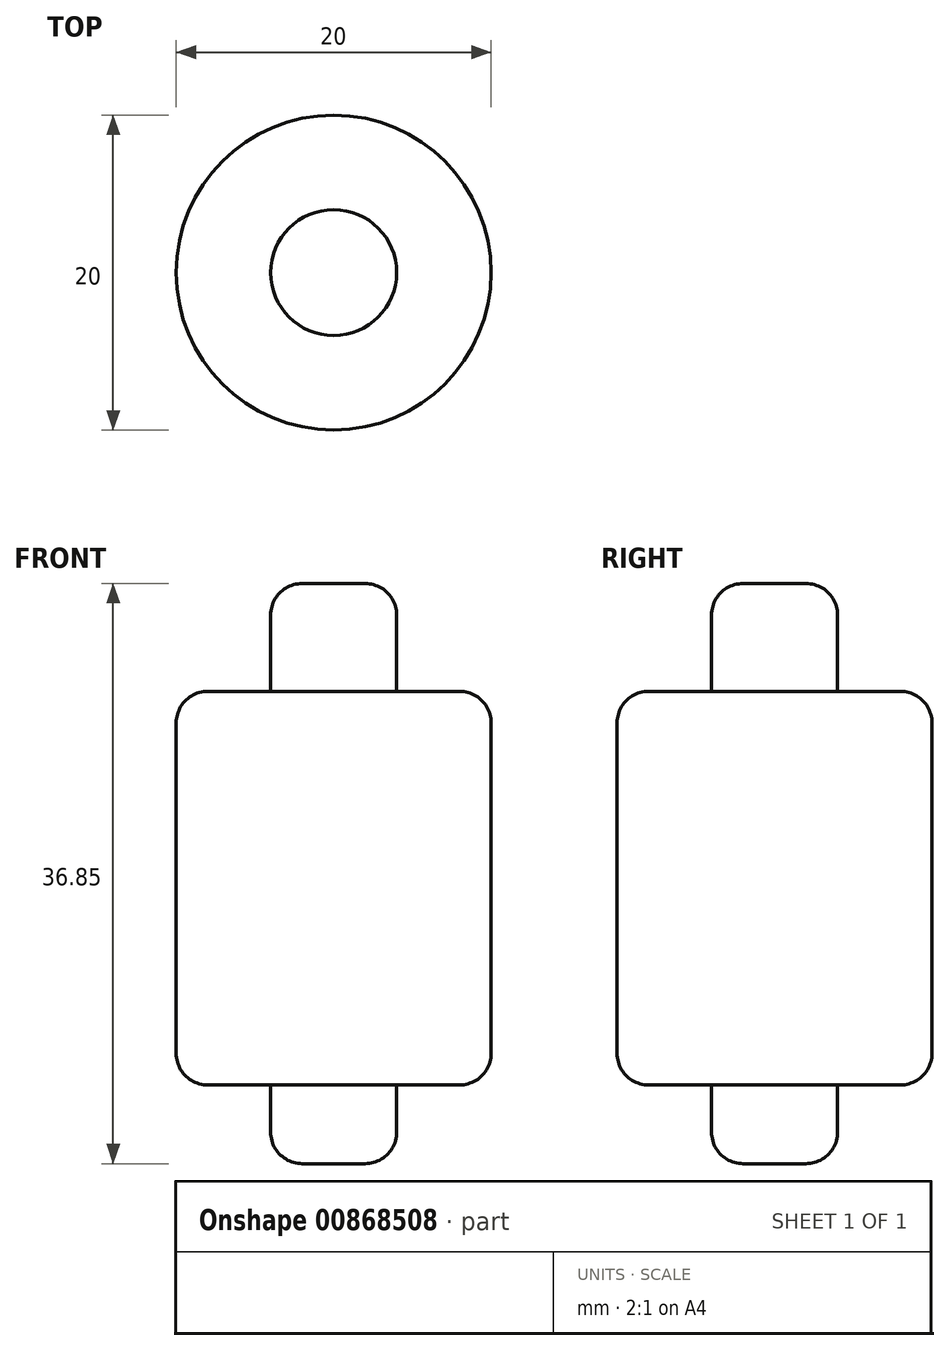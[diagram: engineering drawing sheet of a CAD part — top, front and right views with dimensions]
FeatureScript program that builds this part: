
annotation { "Feature Type Name" : "Feature", "Feature Type Description" : "" }
export const myFeature = defineFeature(function(context is Context, id is Id, definition is map)
    precondition{}
    {
        {
            var Q0;
            Q0=qCreatedBy(makeId("Front.planeOp"),FACE);
            var sketch = newSketch(context, id + "F0", { "sketchPlane" : qUnion([Q0])});
            skLineSegment(sketch, "E0", {"start": v(0, 0) * mm, "end": v(-4, 0) * mm});
            skLineSegment(sketch, "E1", {"start": v(-4, 0) * mm, "end": v(-4, 5) * mm});
            skLineSegment(sketch, "E2", {"start": v(-4, 5) * mm, "end": v(-10, 5) * mm});
            skLineSegment(sketch, "E3", {"start": v(-10, 5) * mm, "end": v(-10, 30) * mm});
            skLineSegment(sketch, "E4", {"start": v(-10, 30) * mm, "end": v(-4, 30) * mm});
            skLineSegment(sketch, "E5", {"start": v(-4, 30) * mm, "end": v(-4, 36.85) * mm});
            skLineSegment(sketch, "E6", {"start": v(-4, 36.85) * mm, "end": v(0, 36.85) * mm});
            skLineSegment(sketch, "E7", {"start": v(0, 36.85) * mm, "end": v(0, 0) * mm});
            skSolve(sketch);
        }
        {
            var Q0;
            Q0=makeQuery(id+"F0.imprint","IMPRINT",FACE,{"disambiguationData":[TD([[makeQuery(id+"F0.imprint","IMPRINT",EDGE,{"derivedFrom":sQuery(id+"F0.wireOp",EDGE,"E0")}),-1.0]])]});
            var Q1;
            Q1=sQuery(id+"F0.wireOp",EDGE,"E7");
            revolve(context, id + "F1", {"surfaceOperationType" : NewSurfaceOperationType.NEW, "entities" : qUnion([Q0]), "axis" : qUnion([Q1]), "revolveType" : RevolveType.FULL});
        }
        {
            var Q0;
            Q0=makeQuery(id+"F1.opRevolve","SWEPT_EDGE",EDGE,{"disambiguationData":[OSD([sQuery(id+"F0.wireOp",EDGE,"E3"),sQuery(id+"F0.wireOp",EDGE,"E4")])]});
            var Q1;
            Q1=makeQuery(id+"F1.opRevolve","SWEPT_EDGE",EDGE,{"disambiguationData":[OSD([sQuery(id+"F0.wireOp",EDGE,"E2"),sQuery(id+"F0.wireOp",EDGE,"E3")])]});
            var Q2;
            Q2=makeQuery(id+"F1.opRevolve","SWEPT_EDGE",EDGE,{"disambiguationData":[OSD([sQuery(id+"F0.wireOp",EDGE,"E0"),sQuery(id+"F0.wireOp",EDGE,"E1")])]});
            var Q3;
            Q3=makeQuery(id+"F1.opRevolve","SWEPT_EDGE",EDGE,{"disambiguationData":[OSD([sQuery(id+"F0.wireOp",EDGE,"E5"),sQuery(id+"F0.wireOp",EDGE,"E6")])]});
            fillet(context, id + "F2", {"entities" : qUnion([Q0, Q1, Q2, Q3]), "radius" : 2 * mm, "tangentPropagation" : true, "allowEdgeOverflow" : false});
        }
    });
